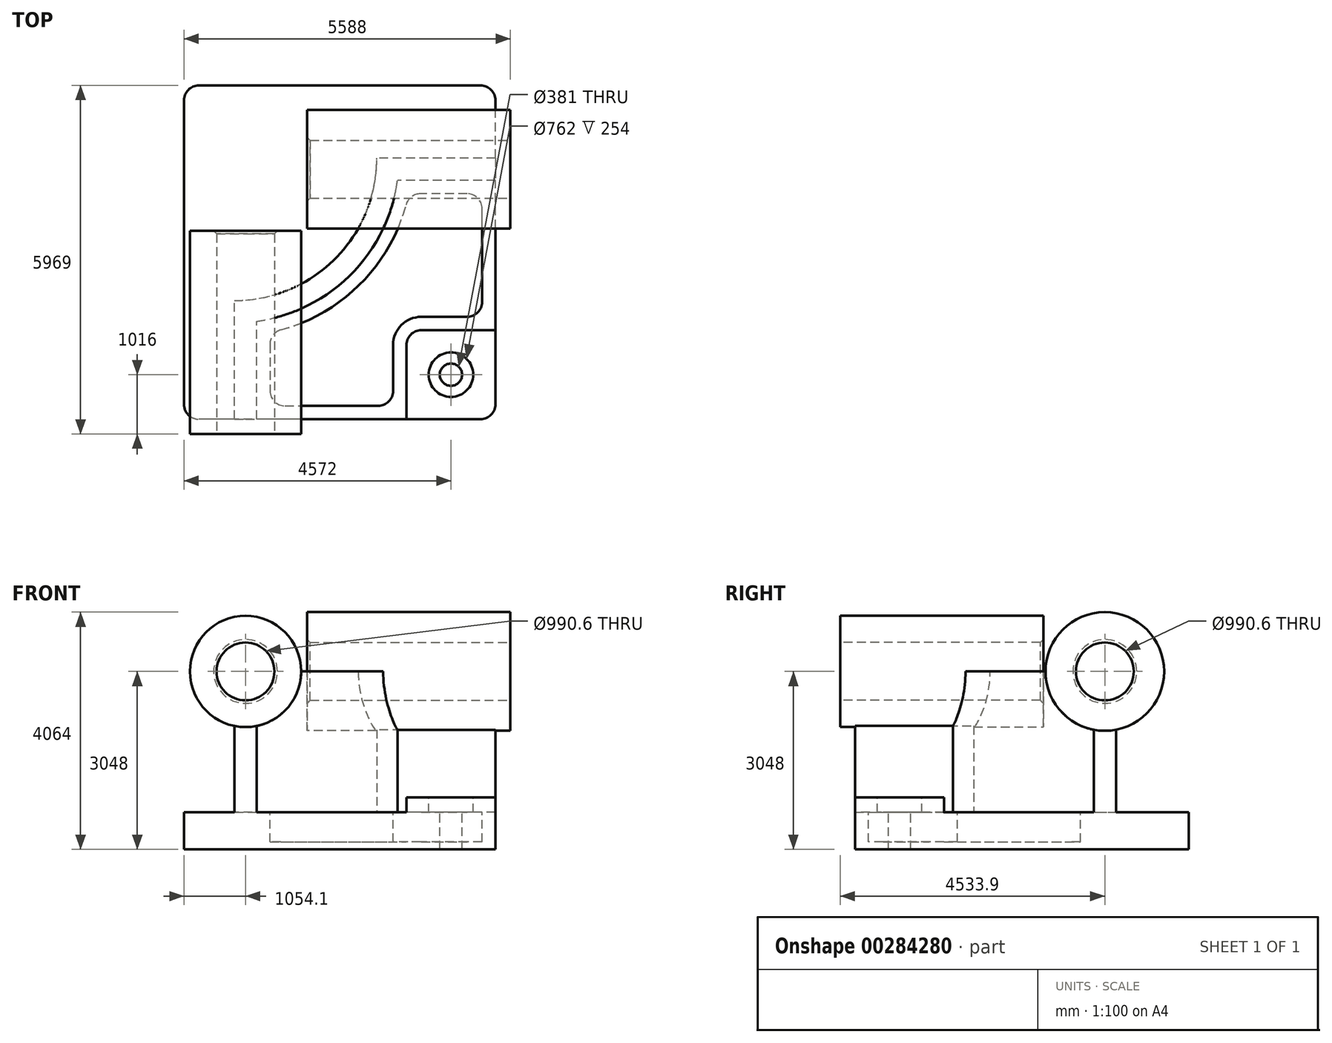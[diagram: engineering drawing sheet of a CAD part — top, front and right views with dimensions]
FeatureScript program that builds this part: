
annotation { "Feature Type Name" : "Feature", "Feature Type Description" : "" }
export const myFeature = defineFeature(function(context is Context, id is Id, definition is map)
    precondition{}
    {
        {
            var Q0;
            Q0=qCreatedBy(makeId("Top.planeOp"),FACE);
            var sketch = newSketch(context, id + "F0", { "sketchPlane" : qUnion([Q0])});
            skLineSegment(sketch, "E0.bottom", {"start": v(2667, -2857.5) * mm, "end": v(-2667, -2857.5) * mm});
            skLineSegment(sketch, "E0.top", {"start": v(2667, 2857.5) * mm, "end": v(-2667, 2857.5) * mm});
            skLineSegment(sketch, "E0.left", {"start": v(2667, -2857.5) * mm, "end": v(2667, 2857.5) * mm});
            skLineSegment(sketch, "E0.right", {"start": v(-2667, -2857.5) * mm, "end": v(-2667, 2857.5) * mm});
            skPoint(sketch, "E0.middle", {"position": v(0, 0) * mm});
            skSolve(sketch);
        }
        {
            var Q0;
            Q0 = qSketchRegion(id + "F0", true);
            extrude(context, id + "F1", {"entities" : qUnion([Q0]), "depth" : 635 * mm});
        }
        {
            var Q0;
            Q0=makeQuery(id+"F1.opExtrude","CAP_FACE",FACE,{"disambiguationData":[OSD([sQuery(id+"F0.wireOp",EDGE,"E0.bottom"),sQuery(id+"F0.wireOp",EDGE,"E0.top"),sQuery(id+"F0.wireOp",EDGE,"E0.left"),sQuery(id+"F0.wireOp",EDGE,"E0.right")])],"isStart":false});
            var sketch = newSketch(context, id + "F2", { "sketchPlane" : qUnion([Q0])});
            skLineSegment(sketch, "E1", {"start": v(-1803.4, -2857.5) * mm, "end": v(-1803.4, -825.5) * mm});
            skLineSegment(sketch, "E2", {"start": v(2667, 1612.9) * mm, "end": v(635, 1612.9) * mm});
            skArc(sketch, "E3", {"start": v(-1803.4, -825.5) * mm, "mid": v(-79.2, -111.3) * mm, "end": v(635, 1612.9) * mm});
            skLineSegment(sketch, "E4", {"start": v(-1803.4, 1612.9) * mm, "end": v(635, 1612.9) * mm, "construction": true});
            skLineSegment(sketch, "E5", {"start": v(-1803.4, 1612.9) * mm, "end": v(-1803.4, -825.5) * mm, "construction": true});
            skLineSegment(sketch, "E6.0", {"start": v(-1422.4, -2857.5) * mm, "end": v(-1422.4, -1180.64) * mm});
            skArc(sketch, "E6.1", {"start": v(-1422.4, -1180.64) * mm, "mid": v(190.22, -380.72) * mm, "end": v(990.14, 1231.9) * mm});
            skLineSegment(sketch, "E6.2", {"start": v(2667, 1231.9) * mm, "end": v(990.14, 1231.9) * mm});
            skLineSegment(sketch, "E7.0", {"start": v(2673.35, -2863.85) * mm, "end": v(2673.35, 2863.85) * mm});
            skLineSegment(sketch, "E7.1", {"start": v(-2673.35, -2863.85) * mm, "end": v(2673.35, -2863.85) * mm});
            skLineSegment(sketch, "E7.2", {"start": v(-2673.35, 2863.85) * mm, "end": v(-2673.35, -2863.85) * mm});
            skLineSegment(sketch, "E7.3", {"start": v(2673.35, 2863.85) * mm, "end": v(-2673.35, 2863.85) * mm});
            skLineSegment(sketch, "E8", {"start": v(2667, 1612.9) * mm, "end": v(2667, 1231.9) * mm});
            skLineSegment(sketch, "E9", {"start": v(-1422.4, -2857.5) * mm, "end": v(-1803.4, -2857.5) * mm});
            skSolve(sketch);
        }
        {
            var Q0;
            Q0=makeQuery(id+"F2.imprint","IMPRINT",FACE,{"disambiguationData":[TD([[makeQuery(id+"F2.imprint","IMPRINT",EDGE,{"derivedFrom":sQuery(id+"F2.wireOp",EDGE,"E1")}),-1.0]])]});
            extrude(context, id + "F3", {"entities" : qUnion([Q0]), "operationType" : NewBodyOperationType.ADD, "depth" : 2413 * mm});
        }
        {
            var Q0;
            Q0=makeQuery(id+"F3.boolean.opBoolean","MERGE",FACE,{"derivedFrom":[makeQuery(id+"F1.opExtrude","SWEPT_FACE",FACE,{"disambiguationData":[OSD([sQuery(id+"F0.wireOp",EDGE,"E0.bottom")])]}),makeQuery(id+"F3.opExtrude","SWEPT_FACE",FACE,{"disambiguationData":[OSD([sQuery(id+"F2.wireOp",EDGE,"E9")])]})]});
            var sketch = newSketch(context, id + "F4", { "sketchPlane" : qUnion([Q0])});
            skCircle(sketch, "E10", {"center": v(-1612.9, 3048) * mm, "radius": 952.5 * mm});
            skSolve(sketch);
        }
        {
            var Q0;
            Q0 = qSketchRegion(id + "F4", true);
            extrude(context, id + "F5", {"entities" : qUnion([Q0]), "operationType" : NewBodyOperationType.ADD, "depth" : 254 * mm, "hasSecondDirection" : true, "secondDirectionOppositeDirection" : true, "secondDirectionDepth" : 3225.8 * mm});
        }
        {
            var Q0;
            Q0=makeQuery(id+"F3.boolean.opBoolean","MERGE",FACE,{"derivedFrom":[makeQuery(id+"F1.opExtrude","SWEPT_FACE",FACE,{"disambiguationData":[OSD([sQuery(id+"F0.wireOp",EDGE,"E0.left")])]}),makeQuery(id+"F3.opExtrude","SWEPT_FACE",FACE,{"disambiguationData":[OSD([sQuery(id+"F2.wireOp",EDGE,"E8")])]})]});
            var sketch = newSketch(context, id + "F6", { "sketchPlane" : qUnion([Q0])});
            skCircle(sketch, "E11", {"center": v(1422.4, 3048) * mm, "radius": 1016 * mm});
            skSolve(sketch);
        }
        {
            var Q0;
            Q0 = qSketchRegion(id + "F6", true);
            extrude(context, id + "F7", {"entities" : qUnion([Q0]), "operationType" : NewBodyOperationType.ADD, "depth" : 254 * mm, "hasSecondDirection" : true, "secondDirectionOppositeDirection" : true, "secondDirectionDepth" : 3225.8 * mm});
        }
        {
            var Q0;
            {var subQ0=sQuery(id+"F0.wireOp",EDGE,"E0.left");var subQ1=sQuery(id+"F0.wireOp",EDGE,"E0.bottom");Q0=makeQuery(id+"F3.boolean.opBoolean","SPLIT",FACE,{"disambiguationData":[TD([makeQuery(id+"F3.opExtrude","SWEPT_FACE",FACE,{"disambiguationData":[OSD([sQuery(id+"F2.wireOp",EDGE,"E6.0")])]})])],"derivedFrom":makeQuery(id+"F1.opExtrude","CAP_FACE",FACE,{"disambiguationData":[OSD([subQ1,sQuery(id+"F0.wireOp",EDGE,"E0.top"),subQ0,sQuery(id+"F0.wireOp",EDGE,"E0.right")])],"isStart":false})});}
            var sketch = newSketch(context, id + "F8", { "sketchPlane" : qUnion([Q0])});
            skLineSegment(sketch, "E12.bottom", {"start": v(2667, -2857.5) * mm, "end": v(1143, -2857.5) * mm});
            skLineSegment(sketch, "E12.top", {"start": v(2667, -1333.5) * mm, "end": v(1143, -1333.5) * mm});
            skLineSegment(sketch, "E12.left", {"start": v(2667, -2857.5) * mm, "end": v(2667, -1333.5) * mm});
            skLineSegment(sketch, "E12.right", {"start": v(1143, -2857.5) * mm, "end": v(1143, -1333.5) * mm});
            skSolve(sketch);
        }
        {
            var Q0;
            Q0 = qSketchRegion(id + "F8", true);
            extrude(context, id + "F9", {"entities" : qUnion([Q0]), "operationType" : NewBodyOperationType.ADD, "depth" : 254 * mm});
        }
        {
            var Q0;
            Q0=makeQuery(id+"F9.opExtrude","SWEPT_EDGE",EDGE,{"disambiguationData":[OSD([sQuery(id+"F8.wireOp",EDGE,"E12.top"),sQuery(id+"F8.wireOp",EDGE,"E12.right")])]});
            fillet(context, id + "F10", {"entities" : qUnion([Q0]), "radius" : 254 * mm, "tangentPropagation" : true, "allowEdgeOverflow" : false});
        }
        {
            var Q0;
            {var subQ0=sQuery(id+"F0.wireOp",EDGE,"E0.left");var subQ1=sQuery(id+"F0.wireOp",EDGE,"E0.bottom");Q0=makeQuery(id+"F3.boolean.opBoolean","SPLIT",FACE,{"disambiguationData":[TD([makeQuery(id+"F3.opExtrude","SWEPT_FACE",FACE,{"disambiguationData":[OSD([sQuery(id+"F2.wireOp",EDGE,"E6.0")])]})])],"derivedFrom":makeQuery(id+"F1.opExtrude","CAP_FACE",FACE,{"disambiguationData":[OSD([subQ1,sQuery(id+"F0.wireOp",EDGE,"E0.top"),subQ0,sQuery(id+"F0.wireOp",EDGE,"E0.right")])],"isStart":false})});}
            var sketch = newSketch(context, id + "F11", { "sketchPlane" : qUnion([Q0])});
            skLineSegment(sketch, "E13.0", {"start": v(-1193.8, -1373.52) * mm, "end": v(-1193.8, -2628.9) * mm});
            skArc(sketch, "E13.1", {"start": v(1183.02, 1003.3) * mm, "mid": v(351.86, -542.36) * mm, "end": v(-1193.8, -1373.52) * mm});
            skLineSegment(sketch, "E13.2", {"start": v(-1193.8, -2628.9) * mm, "end": v(914.4, -2628.9) * mm});
            skLineSegment(sketch, "E13.3", {"start": v(2438.4, 1003.3) * mm, "end": v(1183.02, 1003.3) * mm});
            skLineSegment(sketch, "E13.4", {"start": v(914.4, -2628.9) * mm, "end": v(914.4, -1587.5) * mm});
            skArc(sketch, "E13.5", {"start": v(914.4, -1587.5) * mm, "mid": v(1055.75, -1246.25) * mm, "end": v(1397, -1104.9) * mm});
            skLineSegment(sketch, "E13.6", {"start": v(1397, -1104.9) * mm, "end": v(2438.4, -1104.9) * mm});
            skLineSegment(sketch, "E13.7", {"start": v(2438.4, -1104.9) * mm, "end": v(2438.4, 1003.3) * mm});
            skSolve(sketch);
        }
        {
            var Q0;
            Q0=makeQuery(id+"F11.imprint","IMPRINT",FACE,{"disambiguationData":[TD([[makeQuery(id+"F11.imprint","IMPRINT",EDGE,{"derivedFrom":sQuery(id+"F11.wireOp",EDGE,"E13.0")}),1.0]])]});
            extrude(context, id + "F12", {"entities" : qUnion([Q0]), "operationType" : NewBodyOperationType.REMOVE, "oppositeDirection" : true, "depth" : 508 * mm});
        }
        {
            var Q0;
            Q0=makeQuery(id+"F9.opExtrude","CAP_FACE",FACE,{"disambiguationData":[OSD([sQuery(id+"F8.wireOp",EDGE,"E12.bottom"),sQuery(id+"F8.wireOp",EDGE,"E12.top"),sQuery(id+"F8.wireOp",EDGE,"E12.left"),sQuery(id+"F8.wireOp",EDGE,"E12.right")])],"isStart":false});
            var sketch = newSketch(context, id + "F13", { "sketchPlane" : qUnion([Q0])});
            skCircle(sketch, "E14", {"center": v(1905, -2095.5) * mm, "radius": 381 * mm});
            skSolve(sketch);
        }
        {
            var Q0;
            Q0=sQuery(id+"F13.wireOp",VERTEX,"E14.center");
            var Q1;
            Q1=makeQuery(id+"F1.opExtrude","SWEPT_BODY",BODY,{"disambiguationData":[OSD([sQuery(id+"F0.wireOp",EDGE,"E0.bottom"),sQuery(id+"F0.wireOp",EDGE,"E0.top"),sQuery(id+"F0.wireOp",EDGE,"E0.left"),sQuery(id+"F0.wireOp",EDGE,"E0.right")])]});
            hole(context, id + "F14", {"style" : HoleStyle.C_BORE, "endStyle" : HoleEndStyle.THROUGH, "holeDiameter" : 381 * mm, "cBoreDiameter" : 762 * mm, "cBoreDepth" : 254 * mm, "isTappedThrough" : true, "tappedDepth" : 12.7 * mm, "tapClearance" : 3, "startFromSketch" : true, "locations" : qUnion([Q0]), "scope" : qUnion([Q1])});
        }
        {
            var Q0;
            Q0=makeQuery(id+"F12.boolean.opBoolean","COPY",EDGE,{"derivedFrom":makeQuery(id+"F12.opExtrude","SWEPT_EDGE",EDGE,{"disambiguationData":[OSD([sQuery(id+"F11.wireOp",EDGE,"E13.0"),sQuery(id+"F11.wireOp",EDGE,"E13.1")])]})});
            var Q1;
            Q1=makeQuery(id+"F12.boolean.opBoolean","COPY",EDGE,{"derivedFrom":makeQuery(id+"F12.opExtrude","SWEPT_EDGE",EDGE,{"disambiguationData":[OSD([sQuery(id+"F11.wireOp",EDGE,"E13.1"),sQuery(id+"F11.wireOp",EDGE,"E13.3")])]})});
            var Q2;
            Q2=makeQuery(id+"F12.boolean.opBoolean","COPY",EDGE,{"derivedFrom":makeQuery(id+"F12.opExtrude","SWEPT_EDGE",EDGE,{"disambiguationData":[OSD([sQuery(id+"F11.wireOp",EDGE,"E13.0"),sQuery(id+"F11.wireOp",EDGE,"E13.2")])]})});
            var Q3;
            Q3=makeQuery(id+"F12.boolean.opBoolean","COPY",EDGE,{"derivedFrom":makeQuery(id+"F12.opExtrude","SWEPT_EDGE",EDGE,{"disambiguationData":[OSD([sQuery(id+"F11.wireOp",EDGE,"E13.2"),sQuery(id+"F11.wireOp",EDGE,"E13.4")])]})});
            var Q4;
            Q4=makeQuery(id+"F12.boolean.opBoolean","COPY",EDGE,{"derivedFrom":makeQuery(id+"F12.opExtrude","SWEPT_EDGE",EDGE,{"disambiguationData":[OSD([sQuery(id+"F11.wireOp",EDGE,"E13.6"),sQuery(id+"F11.wireOp",EDGE,"E13.7")])]})});
            var Q5;
            Q5=makeQuery(id+"F12.boolean.opBoolean","COPY",EDGE,{"derivedFrom":makeQuery(id+"F12.opExtrude","SWEPT_EDGE",EDGE,{"disambiguationData":[OSD([sQuery(id+"F11.wireOp",EDGE,"E13.3"),sQuery(id+"F11.wireOp",EDGE,"E13.7")])]})});
            fillet(context, id + "F15", {"entities" : qUnion([Q0, Q1, Q2, Q3, Q4, Q5]), "radius" : 254 * mm, "tangentPropagation" : true, "allowEdgeOverflow" : false});
        }
        {
            var Q0;
            Q0=makeQuery(id+"F5.opExtrude","CAP_FACE",FACE,{"disambiguationData":[OSD([sQuery(id+"F4.wireOp",EDGE,"E10")])],"isStart":false});
            var sketch = newSketch(context, id + "F16", { "sketchPlane" : qUnion([Q0])});
            skCircle(sketch, "E15", {"center": v(-1612.9, 3048) * mm, "radius": 495.3 * mm});
            skSolve(sketch);
        }
        {
            var Q0;
            Q0 = qSketchRegion(id + "F16", true);
            extrude(context, id + "F17", {"entities" : qUnion([Q0]), "operationType" : NewBodyOperationType.REMOVE, "endBound" : BoundingType.THROUGH_ALL, "oppositeDirection" : true, "depth" : 25.4 * mm});
        }
        {
            var Q0;
            Q0=makeQuery(id+"F7.opExtrude","CAP_FACE",FACE,{"disambiguationData":[OSD([sQuery(id+"F6.wireOp",EDGE,"E11")])],"isStart":false});
            var sketch = newSketch(context, id + "F18", { "sketchPlane" : qUnion([Q0])});
            skCircle(sketch, "E16", {"center": v(1422.4, 3048) * mm, "radius": 495.3 * mm});
            skSolve(sketch);
        }
        {
            var Q0;
            Q0 = qSketchRegion(id + "F18", true);
            extrude(context, id + "F19", {"entities" : qUnion([Q0]), "operationType" : NewBodyOperationType.REMOVE, "endBound" : BoundingType.THROUGH_ALL, "oppositeDirection" : true, "depth" : 25.4 * mm});
        }
        {
            var Q0;
            Q0=makeQuery(id+"F17.boolean.opBoolean","COPY",EDGE,{"derivedFrom":makeQuery(id+"F17.opExtrude","CAP_EDGE",EDGE,{"disambiguationData":[OSD([sQuery(id+"F16.wireOp",EDGE,"E15")])],"isStart":true})});
            var Q1;
            Q1=makeQuery(id+"F19.boolean.opBoolean","COPY",EDGE,{"derivedFrom":makeQuery(id+"F19.opExtrude","CAP_EDGE",EDGE,{"disambiguationData":[OSD([sQuery(id+"F18.wireOp",EDGE,"E16")])],"isStart":true})});
            var Q2;
            Q2=makeQuery(id+"F19.boolean.opBoolean","INTERSECT",EDGE,{"derivedFrom":[makeQuery(id+"F7.opExtrude","CAP_FACE",FACE,{"disambiguationData":[OSD([sQuery(id+"F6.wireOp",EDGE,"E11")])],"isStart":true}),makeQuery(id+"F19.opExtrude","SWEPT_FACE",FACE,{"disambiguationData":[OSD([sQuery(id+"F18.wireOp",EDGE,"E16")])]})]});
            var Q3;
            Q3=makeQuery(id+"F17.boolean.opBoolean","INTERSECT",EDGE,{"derivedFrom":[makeQuery(id+"F5.opExtrude","CAP_FACE",FACE,{"disambiguationData":[OSD([sQuery(id+"F4.wireOp",EDGE,"E10")])],"isStart":true}),makeQuery(id+"F17.opExtrude","SWEPT_FACE",FACE,{"disambiguationData":[OSD([sQuery(id+"F16.wireOp",EDGE,"E15")])]})]});
            chamfer(context, id + "F20", {"entities" : qUnion([Q0, Q1, Q2, Q3]), "width" : 50.8 * mm, "tangentPropagation" : true});
        }
        {
            var Q0;
            Q0=makeQuery(id+"F1.opExtrude","SWEPT_EDGE",EDGE,{"disambiguationData":[OSD([sQuery(id+"F0.wireOp",EDGE,"E0.top"),sQuery(id+"F0.wireOp",EDGE,"E0.left")])]});
            var Q1;
            Q1=makeQuery(id+"F9.boolean.opBoolean","MERGE",EDGE,{"derivedFrom":[makeQuery(id+"F1.opExtrude","SWEPT_EDGE",EDGE,{"disambiguationData":[OSD([sQuery(id+"F0.wireOp",EDGE,"E0.bottom"),sQuery(id+"F0.wireOp",EDGE,"E0.left")])]}),makeQuery(id+"F9.opExtrude","SWEPT_EDGE",EDGE,{"disambiguationData":[OSD([sQuery(id+"F8.wireOp",EDGE,"E12.bottom"),sQuery(id+"F8.wireOp",EDGE,"E12.left")])]})]});
            var Q2;
            Q2=makeQuery(id+"F1.opExtrude","SWEPT_EDGE",EDGE,{"disambiguationData":[OSD([sQuery(id+"F0.wireOp",EDGE,"E0.bottom"),sQuery(id+"F0.wireOp",EDGE,"E0.right")])]});
            var Q3;
            Q3=makeQuery(id+"F1.opExtrude","SWEPT_EDGE",EDGE,{"disambiguationData":[OSD([sQuery(id+"F0.wireOp",EDGE,"E0.top"),sQuery(id+"F0.wireOp",EDGE,"E0.right")])]});
            fillet(context, id + "F21", {"entities" : qUnion([Q0, Q1, Q2, Q3]), "radius" : 254 * mm, "tangentPropagation" : true, "allowEdgeOverflow" : false});
        }
    });
